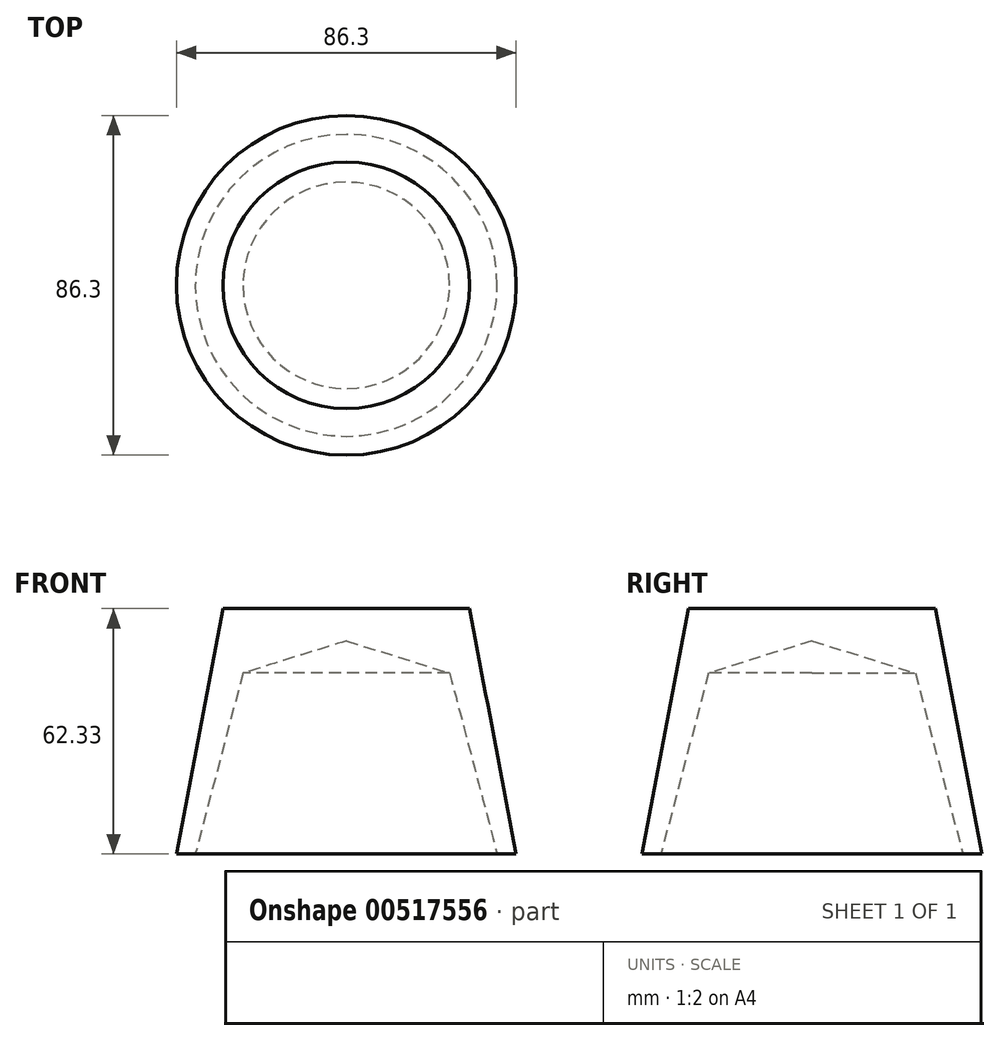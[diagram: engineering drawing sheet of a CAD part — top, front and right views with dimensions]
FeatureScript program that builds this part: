
annotation { "Feature Type Name" : "Feature", "Feature Type Description" : "" }
export const myFeature = defineFeature(function(context is Context, id is Id, definition is map)
    precondition{}
    {
        {
            var Q0;
            Q0=qCreatedBy(makeId("Front.planeOp"),FACE);
            var sketch = newSketch(context, id + "F0", { "sketchPlane" : qUnion([Q0])});
            skLineSegment(sketch, "E0.bottom", {"start": v(43.15, -13.12) * mm, "end": v(-43.15, -13.12) * mm});
            skLineSegment(sketch, "E0.top", {"start": v(43.15, 13.12) * mm, "end": v(-43.15, 13.12) * mm});
            skLineSegment(sketch, "E0.left", {"start": v(43.15, -13.12) * mm, "end": v(43.15, 13.12) * mm});
            skLineSegment(sketch, "E0.right", {"start": v(-43.15, -13.12) * mm, "end": v(-43.15, 13.12) * mm});
            skPoint(sketch, "E0.middle", {"position": v(0, 0) * mm});
            skLineSegment(sketch, "E1", {"start": v(43.15, 13.12) * mm, "end": v(31.3, 75.45) * mm});
            skLineSegment(sketch, "E2", {"start": v(31.3, 75.45) * mm, "end": v(0, 75.45) * mm});
            skLineSegment(sketch, "E3", {"start": v(0, 75.45) * mm, "end": v(0, 67.27) * mm});
            skLineSegment(sketch, "E4", {"start": v(0, 67.27) * mm, "end": v(26.23, 59.09) * mm});
            skLineSegment(sketch, "E5", {"start": v(26.23, 59.09) * mm, "end": v(38.36, 13.12) * mm});
            skSolve(sketch);
        }
        {
            var Q0;
            {var subQ0=sQuery(id+"F0.wireOp",EDGE,"E1");Q0=makeQuery(id+"F0.imprint","IMPRINT",FACE,{"disambiguationData":[TD([[makeQuery(id+"F0.imprint","IMPRINT",EDGE,{"derivedFrom":subQ0}),1.0]])]});}
            var Q1;
            Q1=sQuery(id+"F0.wireOp",EDGE,"E3");
            revolve(context, id + "F1", {"entities" : qUnion([Q0]), "axis" : qUnion([Q1]), "revolveType" : RevolveType.FULL});
        }
    });
